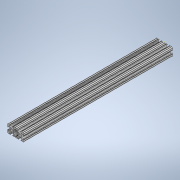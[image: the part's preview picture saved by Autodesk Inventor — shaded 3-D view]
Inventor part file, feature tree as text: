
AUTODESK INVENTOR PART (.ipt)
format: ipt  version: 2020 (Build 240168000, 168)  size: 333,312 bytes
history: native  units: in
note: dims shown in document units (in); Inventor stores cm internally (conversion verified against a paired STEP export)
features: sketch x2, extrude x1
ambient origin geometry x8: Origin, YZ Plane, XZ Plane, XY Plane, X Axis, Y Axis, Z Axis, Center Point
bodies: Solid1 (feature_tree)
feature tree (3):
  extrude  "Extrusion1"  [1 undecoded]
  sketch  "Sketch2"
  sketch  "Sketch1"  dims[d0=18.0in d1=0.0in]
note: 1 required parameter value undecoded (feature->parameter linkage not recoverable at this tier; creation-order binding heuristic only, values carry confidence <= 0.55)
